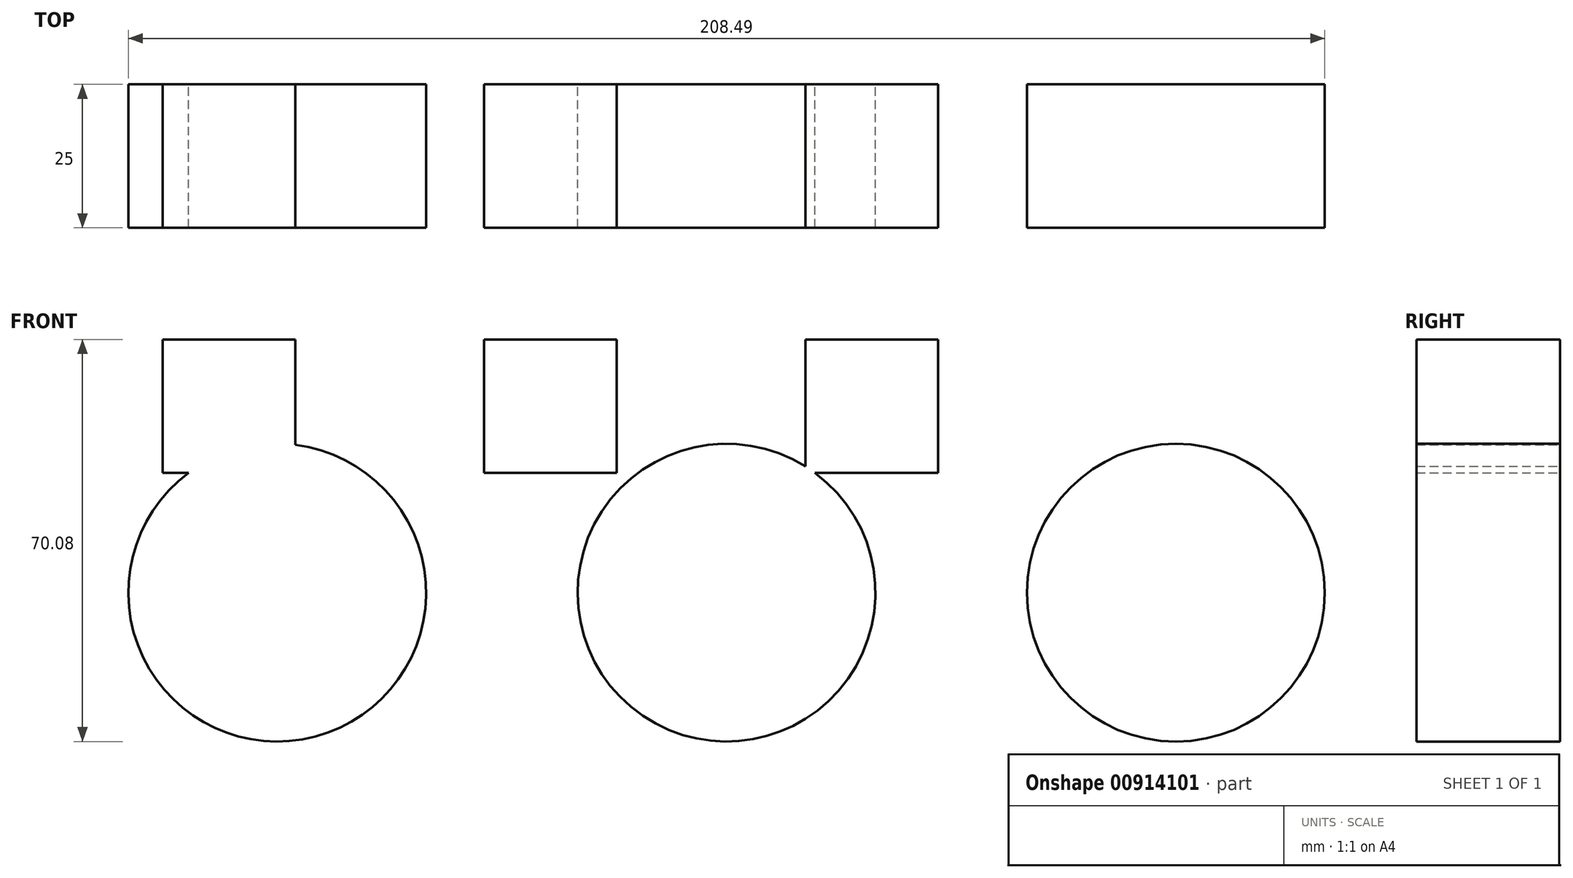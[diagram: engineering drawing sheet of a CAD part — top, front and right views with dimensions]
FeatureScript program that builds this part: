
annotation { "Feature Type Name" : "Feature", "Feature Type Description" : "" }
export const myFeature = defineFeature(function(context is Context, id is Id, definition is map)
    precondition{}
    {
        {
            var Q0;
            Q0=qCreatedBy(makeId("Front.planeOp"),FACE);
            var sketch = newSketch(context, id + "F0", { "sketchPlane" : qUnion([Q0])});
            skCircle(sketch, "E0", {"center": v(-86.25, -17.91) * mm, "radius": 25.95 * mm});
            skCircle(sketch, "E1.1.0.0", {"center": v(-7.95, -17.91) * mm, "radius": 25.95 * mm});
            skCircle(sketch, "E1.2.0.0", {"center": v(70.35, -17.91) * mm, "radius": 25.95 * mm});
            skLineSegment(sketch, "E1.direction1", {"start": v(-86.25, -17.91) * mm, "end": v(-7.95, -17.91) * mm, "construction": true});
            skSolve(sketch);
        }
        {
            var Q0;
            Q0=qCreatedBy(makeId("Front.planeOp"),FACE);
            var sketch = newSketch(context, id + "F1", { "sketchPlane" : qUnion([Q0])});
            skLineSegment(sketch, "E2.bottom", {"start": v(-106.21, 26.22) * mm, "end": v(-83.12, 26.22) * mm});
            skLineSegment(sketch, "E2.top", {"start": v(-106.21, 2.95) * mm, "end": v(-83.12, 2.95) * mm});
            skLineSegment(sketch, "E2.left", {"start": v(-106.21, 26.22) * mm, "end": v(-106.21, 2.95) * mm});
            skLineSegment(sketch, "E2.right", {"start": v(-83.12, 26.22) * mm, "end": v(-83.12, 2.95) * mm});
            skLineSegment(sketch, "E3.1.0.0", {"start": v(-50.21, 2.95) * mm, "end": v(-27.12, 2.95) * mm});
            skLineSegment(sketch, "E3.1.0.1", {"start": v(-50.21, 26.22) * mm, "end": v(-27.12, 26.22) * mm});
            skLineSegment(sketch, "E3.1.0.2", {"start": v(-27.12, 26.22) * mm, "end": v(-27.12, 2.95) * mm});
            skLineSegment(sketch, "E3.1.0.3", {"start": v(-50.21, 26.22) * mm, "end": v(-50.21, 2.95) * mm});
            skLineSegment(sketch, "E3.2.0.0", {"start": v(5.79, 2.95) * mm, "end": v(28.88, 2.95) * mm});
            skLineSegment(sketch, "E3.2.0.1", {"start": v(5.79, 26.22) * mm, "end": v(28.88, 26.22) * mm});
            skLineSegment(sketch, "E3.2.0.2", {"start": v(28.88, 26.22) * mm, "end": v(28.88, 2.95) * mm});
            skLineSegment(sketch, "E3.2.0.3", {"start": v(5.79, 26.22) * mm, "end": v(5.79, 2.95) * mm});
            skLineSegment(sketch, "E3.direction1", {"start": v(-106.21, 2.95) * mm, "end": v(-50.21, 2.95) * mm, "construction": true});
            skSolve(sketch);
        }
        {
            var Q0;
            Q0=qCreatedBy(makeId("Front.planeOp"),FACE);
            var sketch = newSketch(context, id + "F2", { "sketchPlane" : qUnion([Q0])});
            skLineSegment(sketch, "E4.0", {"start": v(5.79, 2.95) * mm, "end": v(28.88, 2.95) * mm});
            skLineSegment(sketch, "E4.1", {"start": v(-27.12, 26.22) * mm, "end": v(-27.12, 2.95) * mm});
            skLineSegment(sketch, "E4.2", {"start": v(-50.21, 26.22) * mm, "end": v(-50.21, 2.95) * mm});
            skLineSegment(sketch, "E4.3", {"start": v(-50.21, 2.95) * mm, "end": v(-27.12, 2.95) * mm});
            skCircle(sketch, "E4.4", {"center": v(70.35, -17.91) * mm, "radius": 25.95 * mm});
            skLineSegment(sketch, "E4.5", {"start": v(-83.12, 26.22) * mm, "end": v(-83.12, 2.95) * mm});
            skCircle(sketch, "E4.6", {"center": v(-7.95, -17.91) * mm, "radius": 25.95 * mm});
            skCircle(sketch, "E4.7", {"center": v(-86.25, -17.91) * mm, "radius": 25.95 * mm});
            skLineSegment(sketch, "E4.8", {"start": v(-106.21, 2.95) * mm, "end": v(-83.12, 2.95) * mm});
            skLineSegment(sketch, "E4.9", {"start": v(-86.25, -17.91) * mm, "end": v(-7.95, -17.91) * mm});
            skLineSegment(sketch, "E4.10", {"start": v(5.79, 26.22) * mm, "end": v(28.88, 26.22) * mm});
            skLineSegment(sketch, "E4.11", {"start": v(28.88, 26.22) * mm, "end": v(28.88, 2.95) * mm});
            skLineSegment(sketch, "E4.12", {"start": v(5.79, 26.22) * mm, "end": v(5.79, 2.95) * mm});
            skLineSegment(sketch, "E4.13", {"start": v(-106.21, 2.95) * mm, "end": v(-50.21, 2.95) * mm});
            skLineSegment(sketch, "E5.0", {"start": v(-50.21, 26.22) * mm, "end": v(-27.12, 26.22) * mm});
            skLineSegment(sketch, "E6.0", {"start": v(-106.21, 26.22) * mm, "end": v(-83.12, 26.22) * mm});
            skLineSegment(sketch, "E7.0", {"start": v(-106.21, 26.22) * mm, "end": v(-106.21, 2.95) * mm});
            skSolve(sketch);
        }
        {
            var Q0;
            Q0 = qSketchRegion(id + "F2", true);
            extrude(context, id + "F3", {"entities" : qUnion([Q0]), "depth" : 25 * mm, "offsetDistance" : 25 * mm});
        }
    });
